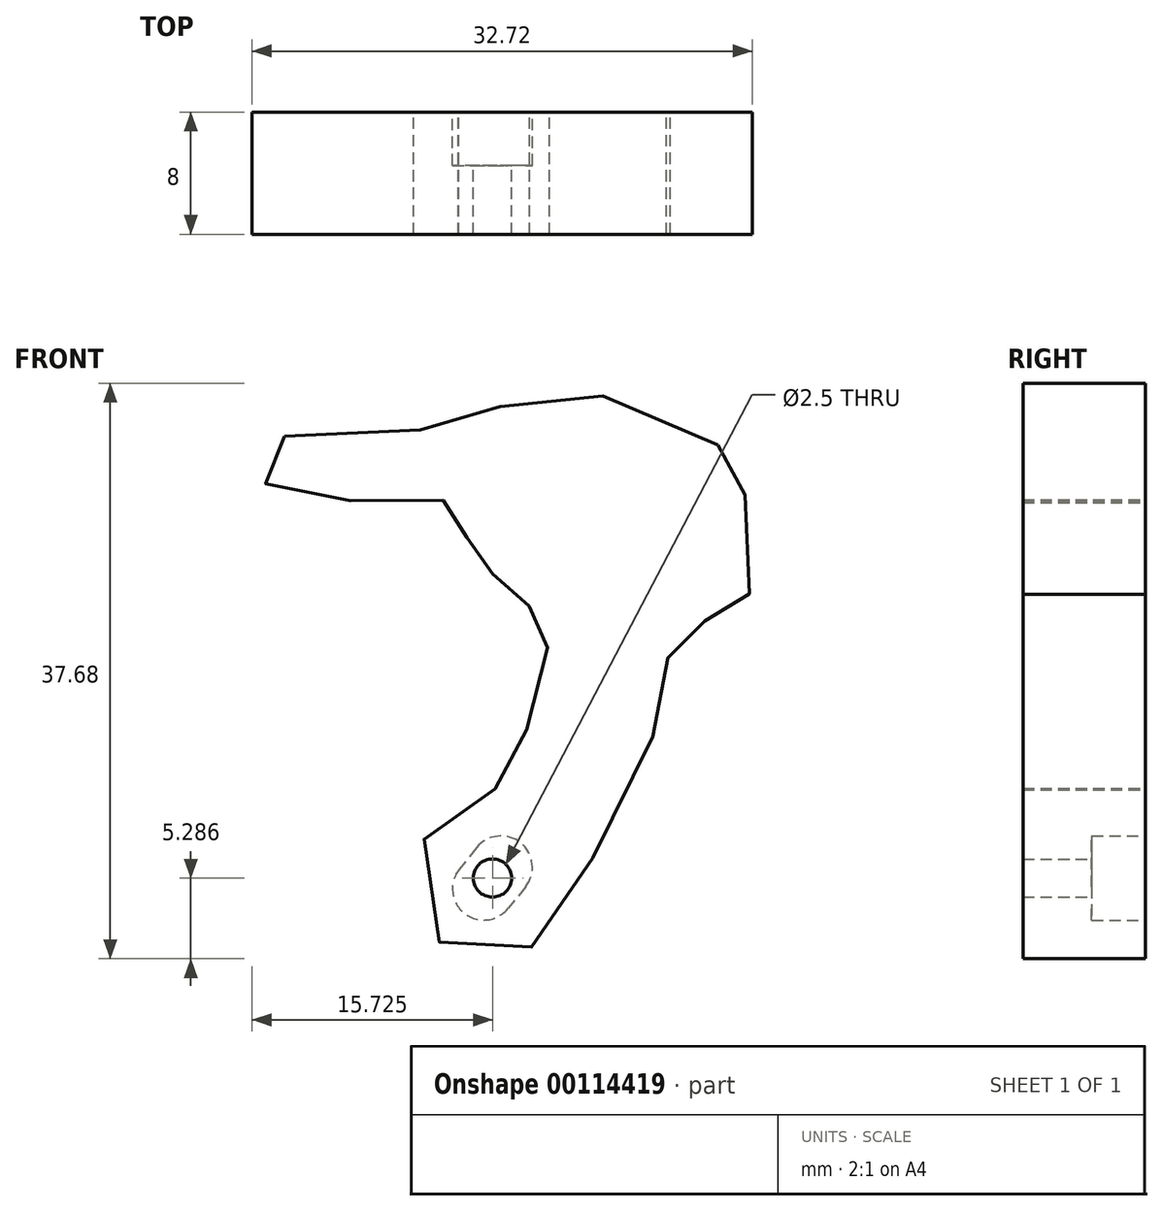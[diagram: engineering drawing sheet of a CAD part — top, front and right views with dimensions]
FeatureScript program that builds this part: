
annotation { "Feature Type Name" : "Feature", "Feature Type Description" : "" }
export const myFeature = defineFeature(function(context is Context, id is Id, definition is map)
    precondition{}
    {
        {
            var Q0;
            Q0=qCreatedBy(makeId("Front.planeOp"),FACE);
            var sketch = newSketch(context, id + "F0", { "sketchPlane" : qUnion([Q0])});
            skLineSegment(sketch, "E0", {"start": v(-59, -25.63) * mm, "end": v(-60.12, -27.04) * mm, "construction": true});
            skLineSegment(sketch, "E1", {"start": v(-56.1, -27.95) * mm, "end": v(-57.23, -29.35) * mm, "construction": true});
            skArc(sketch, "E2", {"start": v(-56.1, -27.95) * mm, "mid": v(-56.4, -25.35) * mm, "end": v(-59, -25.63) * mm, "construction": true});
            skArc(sketch, "E3", {"start": v(-60.12, -27.04) * mm, "mid": v(-59.83, -29.64) * mm, "end": v(-57.23, -29.35) * mm, "construction": true});
            skLineSegment(sketch, "E4", {"start": v(-59, -25.63) * mm, "end": v(-56.1, -27.95) * mm, "construction": true});
            skLineSegment(sketch, "E5", {"start": v(-60.12, -27.04) * mm, "end": v(-57.23, -29.35) * mm, "construction": true});
            skFitSpline(sketch, "E6", {"points": [v(-71.73, 1.43) * mm, v(-73.84, 0) * mm, v(-72.14, -2.28) * mm, v(-67.76, -2.8) * mm, v(-62.59, -2.88) * mm, v(-60.39, -2.88) * mm, v(-60.34, -4.17) * mm, v(-59.13, -5.7) * mm, v(-58.33, -5.95) * mm, v(-58.08, -7.73) * mm, v(-56.86, -9.14) * mm, v(-55.8, -9.49) * mm, v(-55.67, -10.61) * mm, v(-55.05, -11.96) * mm, v(-54.42, -12.55) * mm, v(-54.95, -14.8) * mm, v(-57.08, -21.4) * mm, v(-57.49, -21.72) * mm, v(-59.05, -21.7) * mm, v(-63.06, -26.1) * mm, v(-61.34, -31.9) * mm, v(-56.24, -32.36) * mm, v(-52.86, -28.64) * mm, v(-48.1, -19.2) * mm, v(-46.48, -14.74) * mm, v(-46.74, -12.47) * mm, v(-46.5, -11.96) * mm, v(-43.97, -10.43) * mm, v(-43, -9.05) * mm, v(-41.26, -8.89) * mm, v(-41.13, -8.42) * mm, v(-41.84, 0) * mm, v(-42.2, 0.78) * mm, v(-44.83, 1.15) * mm, v(-54.03, 4.9) * mm, v(-58.5, 2.7) * mm, v(-61.75, 1.86) * mm, v(-71.73, 1.43) * mm]});
            skArc(sketch, "E7.0", {"start": v(-55.95, -28.07) * mm, "mid": v(-56.27, -25.2) * mm, "end": v(-59.15, -25.51) * mm});
            skLineSegment(sketch, "E7.1", {"start": v(-55.95, -28.07) * mm, "end": v(-57.08, -29.48) * mm});
            skArc(sketch, "E7.2", {"start": v(-60.28, -26.92) * mm, "mid": v(-59.96, -29.8) * mm, "end": v(-57.08, -29.48) * mm});
            skLineSegment(sketch, "E7.3", {"start": v(-59.15, -25.51) * mm, "end": v(-60.28, -26.92) * mm});
            skSolve(sketch);
        }
        {
            var Q0;
            Q0=makeQuery(id+"F0.imprint","IMPRINT",FACE,{"disambiguationData":[TD([[makeQuery(id+"F0.imprint","IMPRINT",EDGE,{"derivedFrom":sQuery(id+"F0.wireOp",EDGE,"E7.0")}),1.0]])]});
            var Q1;
            Q1=makeQuery(id+"F0.imprint","IMPRINT",FACE,{"disambiguationData":[TD([[makeQuery(id+"F0.imprint","IMPRINT",EDGE,{"derivedFrom":sQuery(id+"F0.wireOp",EDGE,"E6")}),1.0]])]});
            extrude(context, id + "F1", {"entities" : qUnion([Q0, Q1]), "depth" : 8 * mm});
        }
        {
            var Q0;
            Q0=makeQuery(id+"F0.imprint","IMPRINT",FACE,{"disambiguationData":[TD([[makeQuery(id+"F0.imprint","IMPRINT",EDGE,{"derivedFrom":sQuery(id+"F0.wireOp",EDGE,"E7.0")}),1.0]])]});
            extrude(context, id + "F2", {"entities" : qUnion([Q0]), "operationType" : NewBodyOperationType.REMOVE, "depth" : 3.5 * mm});
        }
        {
            var Q0;
            Q0=makeQuery(id+"F2.boolean.opBoolean","COPY",FACE,{"derivedFrom":makeQuery(id+"F2.opExtrude","CAP_FACE",FACE,{"disambiguationData":[OSD([sQuery(id+"F0.wireOp",EDGE,"E7.0"),sQuery(id+"F0.wireOp",EDGE,"E7.1"),sQuery(id+"F0.wireOp",EDGE,"E7.2"),sQuery(id+"F0.wireOp",EDGE,"E7.3")])],"isStart":false})});
            var sketch = newSketch(context, id + "F3", { "sketchPlane" : qUnion([Q0])});
            skLineSegment(sketch, "E8", {"start": v(59.72, -26.21) * mm, "end": v(56.51, -28.77) * mm, "construction": true});
            skCircle(sketch, "E9", {"center": v(58.11, -27.5) * mm, "radius": 1.25 * mm});
            skSolve(sketch);
        }
        {
            var Q0;
            Q0=makeQuery(id+"F3.imprint","IMPRINT",FACE,{"disambiguationData":[TD([[makeQuery(id+"F3.imprint","IMPRINT",EDGE,{"derivedFrom":sQuery(id+"F3.wireOp",EDGE,"E9")}),1.0]])]});
            extrude(context, id + "F4", {"entities" : qUnion([Q0]), "operationType" : NewBodyOperationType.REMOVE, "endBound" : BoundingType.THROUGH_ALL, "oppositeDirection" : true, "depth" : 25 * mm});
        }
    });
